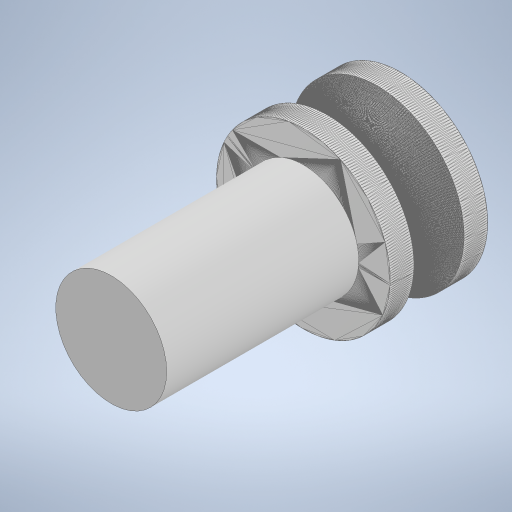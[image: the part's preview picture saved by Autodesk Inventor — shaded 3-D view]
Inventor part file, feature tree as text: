
AUTODESK INVENTOR PART (.ipt)
format: ipt  version: 2024 (Build 280153000, 153)  size: 1,423,872 bytes
history: native  units: mm
features: other x3, extrude x2, sketch x2
ambient origin geometry x8: Origin, YZ Plane, XZ Plane, XY Plane, X Axis, Y Axis, Z Axis, Center Point
bodies: Body1 (feature_tree)
feature tree (7):
  other  "ソリッド1"
  other  "BBbearing1"
  extrude  "押し出し1"  Depth=17.75mm TaperAngle=0.0deg
  extrude  "押し出し2"  Depth=4.0mm
  sketch  "スケッチ1"
  sketch  "スケッチ2"
  other  "メッシュ フィーチャ1"
